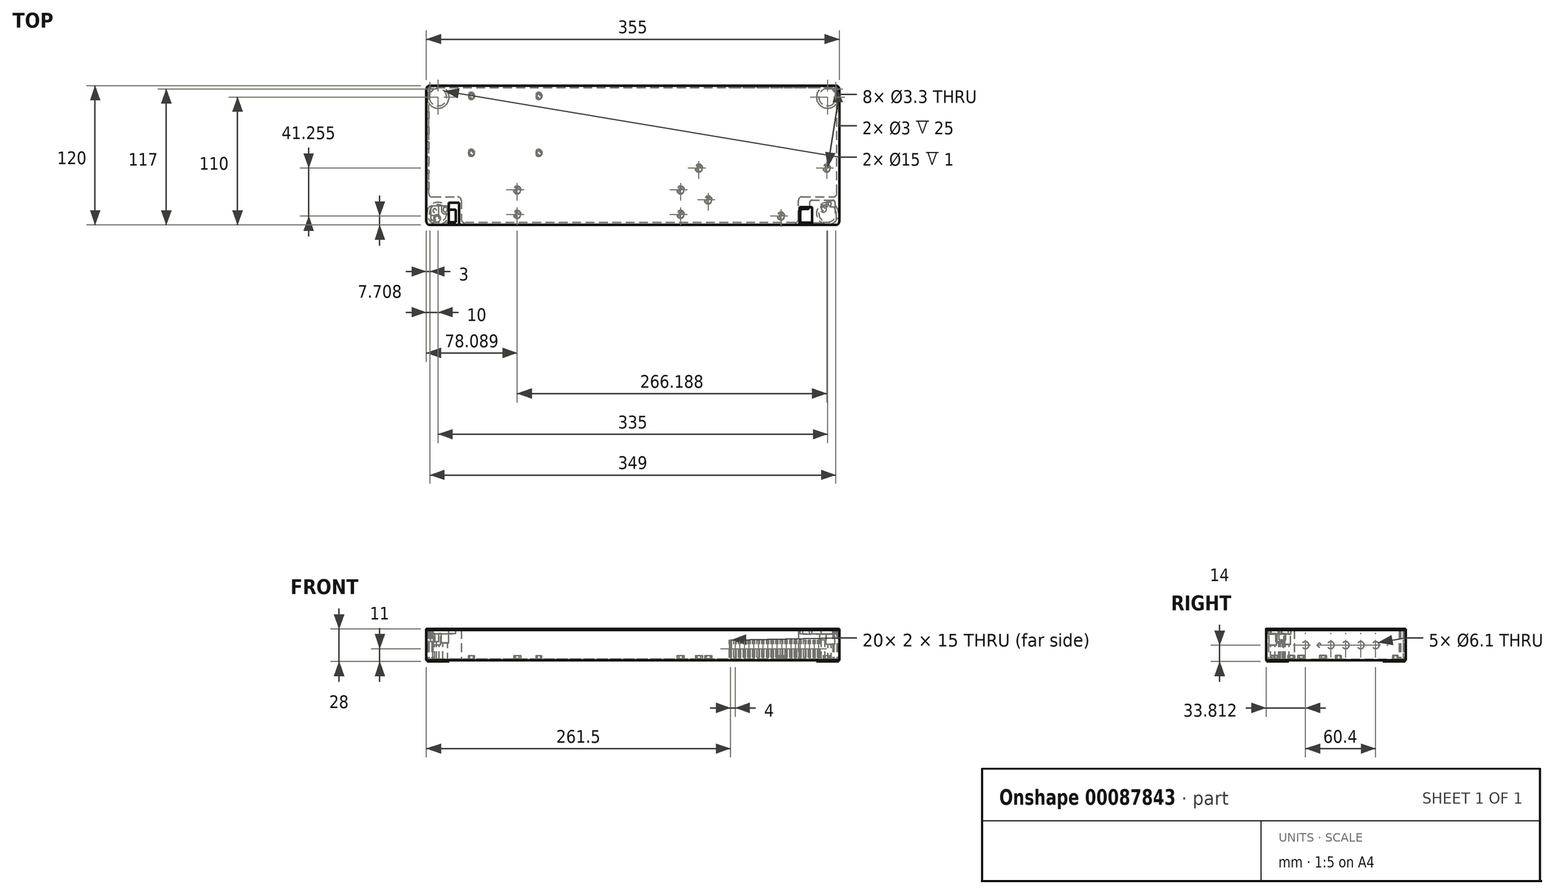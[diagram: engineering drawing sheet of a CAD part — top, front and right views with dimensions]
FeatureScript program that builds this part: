
annotation { "Feature Type Name" : "Feature", "Feature Type Description" : "" }
export const myFeature = defineFeature(function(context is Context, id is Id, definition is map)
    precondition{}
    {
        {
            var Q0;
            Q0=qCreatedBy(makeId("Top.planeOp"),FACE);
            var sketch = newSketch(context, id + "F0", { "sketchPlane" : qUnion([Q0])});
            skLineSegment(sketch, "E0.bottom", {"start": v(174.5, -60) * mm, "end": v(-174.5, -60) * mm});
            skLineSegment(sketch, "E0.top", {"start": v(174.5, 60) * mm, "end": v(-174.5, 60) * mm});
            skLineSegment(sketch, "E0.left", {"start": v(177.5, -57) * mm, "end": v(177.5, 57) * mm});
            skLineSegment(sketch, "E0.right", {"start": v(-177.5, -57) * mm, "end": v(-177.5, 57) * mm});
            skPoint(sketch, "E0.middle", {"position": v(0, 0) * mm});
            skPoint(sketch, "E1.visualSharp", {"position": v(-177.5, 60) * mm});
            skArc(sketch, "E1.filletArc", {"start": v(-174.5, 60) * mm, "mid": v(-176.62, 59.12) * mm, "end": v(-177.5, 57) * mm});
            skPoint(sketch, "E2.visualSharp", {"position": v(-177.5, -60) * mm});
            skArc(sketch, "E2.filletArc", {"start": v(-177.5, -57) * mm, "mid": v(-176.62, -59.12) * mm, "end": v(-174.5, -60) * mm});
            skPoint(sketch, "E3.visualSharp", {"position": v(177.5, -60) * mm});
            skArc(sketch, "E3.filletArc", {"start": v(174.5, -60) * mm, "mid": v(176.62, -59.12) * mm, "end": v(177.5, -57) * mm});
            skPoint(sketch, "E4.visualSharp", {"position": v(177.5, 60) * mm});
            skArc(sketch, "E4.filletArc", {"start": v(177.5, 57) * mm, "mid": v(176.62, 59.12) * mm, "end": v(174.5, 60) * mm});
            skSolve(sketch);
        }
        {
            var Q0;
            Q0=makeQuery(id+"F0.imprint","IMPRINT",FACE,{"disambiguationData":[TD([[makeQuery(id+"F0.imprint","IMPRINT",EDGE,{"derivedFrom":sQuery(id+"F0.wireOp",EDGE,"E0.bottom")}),-1.0]])]});
            extrude(context, id + "F1", {"entities" : qUnion([Q0]), "depth" : 1 * mm});
        }
        {
            var Q0;
            Q0=makeQuery(id+"F1.opExtrude","CAP_FACE",FACE,{"disambiguationData":[OSD([sQuery(id+"F0.wireOp",EDGE,"E0.bottom"),sQuery(id+"F0.wireOp",EDGE,"E0.top"),sQuery(id+"F0.wireOp",EDGE,"E0.left"),sQuery(id+"F0.wireOp",EDGE,"E0.right"),sQuery(id+"F0.wireOp",EDGE,"E1.filletArc"),sQuery(id+"F0.wireOp",EDGE,"E2.filletArc"),sQuery(id+"F0.wireOp",EDGE,"E3.filletArc"),sQuery(id+"F0.wireOp",EDGE,"E4.filletArc")])],"isStart":false});
            var sketch = newSketch(context, id + "F2", { "sketchPlane" : qUnion([Q0])});
            skLineSegment(sketch, "E5.bottom", {"start": v(174.5, -60) * mm, "end": v(-174.5, -60) * mm});
            skLineSegment(sketch, "E5.top", {"start": v(174.5, 60) * mm, "end": v(-174.5, 60) * mm});
            skLineSegment(sketch, "E5.left", {"start": v(177.5, -57) * mm, "end": v(177.5, 57) * mm});
            skLineSegment(sketch, "E5.right", {"start": v(-177.5, -57) * mm, "end": v(-177.5, 57) * mm});
            skPoint(sketch, "E5.middle", {"position": v(0, 0) * mm});
            skPoint(sketch, "E6.visualSharp", {"position": v(-177.5, 60) * mm});
            skArc(sketch, "E6.filletArc", {"start": v(-174.5, 60) * mm, "mid": v(-176.62, 59.12) * mm, "end": v(-177.5, 57) * mm});
            skPoint(sketch, "E7.visualSharp", {"position": v(-177.5, -60) * mm});
            skArc(sketch, "E7.filletArc", {"start": v(-177.5, -57) * mm, "mid": v(-176.62, -59.12) * mm, "end": v(-174.5, -60) * mm});
            skPoint(sketch, "E8.visualSharp", {"position": v(177.5, -60) * mm});
            skArc(sketch, "E8.filletArc", {"start": v(174.5, -60) * mm, "mid": v(176.62, -59.12) * mm, "end": v(177.5, -57) * mm});
            skPoint(sketch, "E9.visualSharp", {"position": v(177.5, 60) * mm});
            skArc(sketch, "E9.filletArc", {"start": v(177.5, 57) * mm, "mid": v(176.62, 59.12) * mm, "end": v(174.5, 60) * mm});
            skLineSegment(sketch, "E10.1", {"start": v(175.5, -32.82) * mm, "end": v(175.5, 54.5) * mm});
            skLineSegment(sketch, "E10.2", {"start": v(172, 58) * mm, "end": v(-172, 58) * mm});
            skLineSegment(sketch, "E10.5", {"start": v(-175.5, -32.82) * mm, "end": v(-175.5, 54.5) * mm});
            skLineSegment(sketch, "E10.7", {"start": v(139.5, -58) * mm, "end": v(-144.5, -58) * mm});
            skCircle(sketch, "E11", {"center": v(-174.5, 57) * mm, "radius": 1.5 * mm});
            skLineSegment(sketch, "E12", {"start": v(-172, 58) * mm, "end": v(-172, 57) * mm});
            skLineSegment(sketch, "E13", {"start": v(-175.5, 54.5) * mm, "end": v(-174.5, 54.5) * mm});
            skArc(sketch, "E14", {"start": v(-174.5, 54.5) * mm, "mid": v(-172.73, 55.23) * mm, "end": v(-172, 57) * mm});
            skCircle(sketch, "E15", {"center": v(174.5, 57) * mm, "radius": 1.5 * mm});
            skLineSegment(sketch, "E16", {"start": v(175.5, 54.5) * mm, "end": v(174.5, 54.5) * mm});
            skLineSegment(sketch, "E17", {"start": v(172, 58) * mm, "end": v(172, 57) * mm});
            skArc(sketch, "E18", {"start": v(172, 57) * mm, "mid": v(172.73, 55.23) * mm, "end": v(174.5, 54.5) * mm});
            skLineSegment(sketch, "E19", {"start": v(-172.5, -35.82) * mm, "end": v(-150.5, -35.82) * mm});
            skLineSegment(sketch, "E20", {"start": v(-147.5, -38.82) * mm, "end": v(-147.5, -55) * mm});
            skLineSegment(sketch, "E21", {"start": v(142.5, -55) * mm, "end": v(142.5, -38.82) * mm});
            skLineSegment(sketch, "E22", {"start": v(145.5, -35.82) * mm, "end": v(172.5, -35.82) * mm});
            skPoint(sketch, "E23.visualSharp", {"position": v(-175.5, -35.82) * mm});
            skArc(sketch, "E23.filletArc", {"start": v(-175.5, -32.82) * mm, "mid": v(-174.62, -34.94) * mm, "end": v(-172.5, -35.82) * mm});
            skPoint(sketch, "E24.visualSharp", {"position": v(-147.5, -35.82) * mm});
            skArc(sketch, "E24.filletArc", {"start": v(-147.5, -38.82) * mm, "mid": v(-148.38, -36.7) * mm, "end": v(-150.5, -35.82) * mm});
            skPoint(sketch, "E25.visualSharp", {"position": v(-147.5, -58) * mm});
            skArc(sketch, "E25.filletArc", {"start": v(-147.5, -55) * mm, "mid": v(-146.62, -57.12) * mm, "end": v(-144.5, -58) * mm});
            skPoint(sketch, "E26.visualSharp", {"position": v(142.5, -35.82) * mm});
            skArc(sketch, "E26.filletArc", {"start": v(145.5, -35.82) * mm, "mid": v(143.38, -36.7) * mm, "end": v(142.5, -38.82) * mm});
            skPoint(sketch, "E27.visualSharp", {"position": v(175.5, -35.82) * mm});
            skArc(sketch, "E27.filletArc", {"start": v(172.5, -35.82) * mm, "mid": v(174.62, -34.94) * mm, "end": v(175.5, -32.82) * mm});
            skPoint(sketch, "E28.visualSharp", {"position": v(142.5, -58) * mm});
            skArc(sketch, "E28.filletArc", {"start": v(139.5, -58) * mm, "mid": v(141.62, -57.12) * mm, "end": v(142.5, -55) * mm});
            skSolve(sketch);
        }
        {
            var Q0;
            Q0 = qSketchRegion(id + "F2", true);
            extrude(context, id + "F3", {"entities" : qUnion([Q0]), "operationType" : NewBodyOperationType.ADD, "depth" : 25 * mm});
        }
        {
            var Q0;
            Q0=makeQuery(id+"F3.boolean.opBoolean","MERGE",FACE,{"derivedFrom":[makeQuery(id+"F1.opExtrude","SWEPT_FACE",FACE,{"disambiguationData":[OSD([sQuery(id+"F0.wireOp",EDGE,"E0.top")])]}),makeQuery(id+"F3.opExtrude","SWEPT_FACE",FACE,{"disambiguationData":[OSD([sQuery(id+"F2.wireOp",EDGE,"E5.top")])]})]});
            var sketch = newSketch(context, id + "F4", { "sketchPlane" : qUnion([Q0])});
            skLineSegment(sketch, "E29.bottom", {"start": v(-159, 2.5) * mm, "end": v(-161, 2.5) * mm});
            skLineSegment(sketch, "E29.top", {"start": v(-159, 17.5) * mm, "end": v(-161, 17.5) * mm});
            skLineSegment(sketch, "E29.left", {"start": v(-159, 2.5) * mm, "end": v(-159, 17.5) * mm});
            skLineSegment(sketch, "E29.right", {"start": v(-161, 2.5) * mm, "end": v(-161, 17.5) * mm});
            skPoint(sketch, "E29.middle", {"position": v(-160, 10) * mm});
            skLineSegment(sketch, "E30.1.0.0", {"start": v(-157, 2.5) * mm, "end": v(-157, 17.5) * mm});
            skLineSegment(sketch, "E30.1.0.1", {"start": v(-155, 17.5) * mm, "end": v(-157, 17.5) * mm});
            skLineSegment(sketch, "E30.1.0.2", {"start": v(-155, 2.5) * mm, "end": v(-155, 17.5) * mm});
            skLineSegment(sketch, "E30.1.0.3", {"start": v(-155, 2.5) * mm, "end": v(-157, 2.5) * mm});
            skLineSegment(sketch, "E30.2.0.0", {"start": v(-153, 2.5) * mm, "end": v(-153, 17.5) * mm});
            skLineSegment(sketch, "E30.2.0.1", {"start": v(-151, 17.5) * mm, "end": v(-153, 17.5) * mm});
            skLineSegment(sketch, "E30.2.0.2", {"start": v(-151, 2.5) * mm, "end": v(-151, 17.5) * mm});
            skLineSegment(sketch, "E30.2.0.3", {"start": v(-151, 2.5) * mm, "end": v(-153, 2.5) * mm});
            skLineSegment(sketch, "E30.3.0.0", {"start": v(-149, 2.5) * mm, "end": v(-149, 17.5) * mm});
            skLineSegment(sketch, "E30.3.0.1", {"start": v(-147, 17.5) * mm, "end": v(-149, 17.5) * mm});
            skLineSegment(sketch, "E30.3.0.2", {"start": v(-147, 2.5) * mm, "end": v(-147, 17.5) * mm});
            skLineSegment(sketch, "E30.3.0.3", {"start": v(-147, 2.5) * mm, "end": v(-149, 2.5) * mm});
            skLineSegment(sketch, "E30.4.0.0", {"start": v(-145, 2.5) * mm, "end": v(-145, 17.5) * mm});
            skLineSegment(sketch, "E30.4.0.1", {"start": v(-143, 17.5) * mm, "end": v(-145, 17.5) * mm});
            skLineSegment(sketch, "E30.4.0.2", {"start": v(-143, 2.5) * mm, "end": v(-143, 17.5) * mm});
            skLineSegment(sketch, "E30.4.0.3", {"start": v(-143, 2.5) * mm, "end": v(-145, 2.5) * mm});
            skLineSegment(sketch, "E30.5.0.0", {"start": v(-141, 2.5) * mm, "end": v(-141, 17.5) * mm});
            skLineSegment(sketch, "E30.5.0.1", {"start": v(-139, 17.5) * mm, "end": v(-141, 17.5) * mm});
            skLineSegment(sketch, "E30.5.0.2", {"start": v(-139, 2.5) * mm, "end": v(-139, 17.5) * mm});
            skLineSegment(sketch, "E30.5.0.3", {"start": v(-139, 2.5) * mm, "end": v(-141, 2.5) * mm});
            skLineSegment(sketch, "E30.6.0.0", {"start": v(-137, 2.5) * mm, "end": v(-137, 17.5) * mm});
            skLineSegment(sketch, "E30.6.0.1", {"start": v(-135, 17.5) * mm, "end": v(-137, 17.5) * mm});
            skLineSegment(sketch, "E30.6.0.2", {"start": v(-135, 2.5) * mm, "end": v(-135, 17.5) * mm});
            skLineSegment(sketch, "E30.6.0.3", {"start": v(-135, 2.5) * mm, "end": v(-137, 2.5) * mm});
            skLineSegment(sketch, "E30.7.0.0", {"start": v(-133, 2.5) * mm, "end": v(-133, 17.5) * mm});
            skLineSegment(sketch, "E30.7.0.1", {"start": v(-131, 17.5) * mm, "end": v(-133, 17.5) * mm});
            skLineSegment(sketch, "E30.7.0.2", {"start": v(-131, 2.5) * mm, "end": v(-131, 17.5) * mm});
            skLineSegment(sketch, "E30.7.0.3", {"start": v(-131, 2.5) * mm, "end": v(-133, 2.5) * mm});
            skLineSegment(sketch, "E30.8.0.0", {"start": v(-129, 2.5) * mm, "end": v(-129, 17.5) * mm});
            skLineSegment(sketch, "E30.8.0.1", {"start": v(-127, 17.5) * mm, "end": v(-129, 17.5) * mm});
            skLineSegment(sketch, "E30.8.0.2", {"start": v(-127, 2.5) * mm, "end": v(-127, 17.5) * mm});
            skLineSegment(sketch, "E30.8.0.3", {"start": v(-127, 2.5) * mm, "end": v(-129, 2.5) * mm});
            skLineSegment(sketch, "E30.9.0.0", {"start": v(-125, 2.5) * mm, "end": v(-125, 17.5) * mm});
            skLineSegment(sketch, "E30.9.0.1", {"start": v(-123, 17.5) * mm, "end": v(-125, 17.5) * mm});
            skLineSegment(sketch, "E30.9.0.2", {"start": v(-123, 2.5) * mm, "end": v(-123, 17.5) * mm});
            skLineSegment(sketch, "E30.9.0.3", {"start": v(-123, 2.5) * mm, "end": v(-125, 2.5) * mm});
            skLineSegment(sketch, "E30.direction1", {"start": v(-161, 2.5) * mm, "end": v(-157, 2.5) * mm, "construction": true});
            skLineSegment(sketch, "E31.0.10.0", {"start": v(-121, 2.5) * mm, "end": v(-121, 17.5) * mm});
            skLineSegment(sketch, "E31.3.10.0", {"start": v(-119, 17.5) * mm, "end": v(-121, 17.5) * mm});
            skLineSegment(sketch, "E31.6.10.0", {"start": v(-119, 2.5) * mm, "end": v(-119, 17.5) * mm});
            skLineSegment(sketch, "E31.9.10.0", {"start": v(-119, 2.5) * mm, "end": v(-121, 2.5) * mm});
            skLineSegment(sketch, "E31.0.11.0", {"start": v(-117, 2.5) * mm, "end": v(-117, 17.5) * mm});
            skLineSegment(sketch, "E31.3.11.0", {"start": v(-115, 17.5) * mm, "end": v(-117, 17.5) * mm});
            skLineSegment(sketch, "E31.6.11.0", {"start": v(-115, 2.5) * mm, "end": v(-115, 17.5) * mm});
            skLineSegment(sketch, "E31.9.11.0", {"start": v(-115, 2.5) * mm, "end": v(-117, 2.5) * mm});
            skLineSegment(sketch, "E31.0.12.0", {"start": v(-113, 2.5) * mm, "end": v(-113, 17.5) * mm});
            skLineSegment(sketch, "E31.3.12.0", {"start": v(-111, 17.5) * mm, "end": v(-113, 17.5) * mm});
            skLineSegment(sketch, "E31.6.12.0", {"start": v(-111, 2.5) * mm, "end": v(-111, 17.5) * mm});
            skLineSegment(sketch, "E31.9.12.0", {"start": v(-111, 2.5) * mm, "end": v(-113, 2.5) * mm});
            skLineSegment(sketch, "E31.0.13.0", {"start": v(-109, 2.5) * mm, "end": v(-109, 17.5) * mm});
            skLineSegment(sketch, "E31.3.13.0", {"start": v(-107, 17.5) * mm, "end": v(-109, 17.5) * mm});
            skLineSegment(sketch, "E31.6.13.0", {"start": v(-107, 2.5) * mm, "end": v(-107, 17.5) * mm});
            skLineSegment(sketch, "E31.9.13.0", {"start": v(-107, 2.5) * mm, "end": v(-109, 2.5) * mm});
            skLineSegment(sketch, "E31.0.14.0", {"start": v(-105, 2.5) * mm, "end": v(-105, 17.5) * mm});
            skLineSegment(sketch, "E31.3.14.0", {"start": v(-103, 17.5) * mm, "end": v(-105, 17.5) * mm});
            skLineSegment(sketch, "E31.6.14.0", {"start": v(-103, 2.5) * mm, "end": v(-103, 17.5) * mm});
            skLineSegment(sketch, "E31.9.14.0", {"start": v(-103, 2.5) * mm, "end": v(-105, 2.5) * mm});
            skLineSegment(sketch, "E31.0.15.0", {"start": v(-101, 2.5) * mm, "end": v(-101, 17.5) * mm});
            skLineSegment(sketch, "E31.3.15.0", {"start": v(-99, 17.5) * mm, "end": v(-101, 17.5) * mm});
            skLineSegment(sketch, "E31.6.15.0", {"start": v(-99, 2.5) * mm, "end": v(-99, 17.5) * mm});
            skLineSegment(sketch, "E31.9.15.0", {"start": v(-99, 2.5) * mm, "end": v(-101, 2.5) * mm});
            skLineSegment(sketch, "E31.0.16.0", {"start": v(-97, 2.5) * mm, "end": v(-97, 17.5) * mm});
            skLineSegment(sketch, "E31.3.16.0", {"start": v(-95, 17.5) * mm, "end": v(-97, 17.5) * mm});
            skLineSegment(sketch, "E31.6.16.0", {"start": v(-95, 2.5) * mm, "end": v(-95, 17.5) * mm});
            skLineSegment(sketch, "E31.9.16.0", {"start": v(-95, 2.5) * mm, "end": v(-97, 2.5) * mm});
            skLineSegment(sketch, "E31.0.17.0", {"start": v(-93, 2.5) * mm, "end": v(-93, 17.5) * mm});
            skLineSegment(sketch, "E31.3.17.0", {"start": v(-91, 17.5) * mm, "end": v(-93, 17.5) * mm});
            skLineSegment(sketch, "E31.6.17.0", {"start": v(-91, 2.5) * mm, "end": v(-91, 17.5) * mm});
            skLineSegment(sketch, "E31.9.17.0", {"start": v(-91, 2.5) * mm, "end": v(-93, 2.5) * mm});
            skLineSegment(sketch, "E31.0.18.0", {"start": v(-89, 2.5) * mm, "end": v(-89, 17.5) * mm});
            skLineSegment(sketch, "E31.3.18.0", {"start": v(-87, 17.5) * mm, "end": v(-89, 17.5) * mm});
            skLineSegment(sketch, "E31.6.18.0", {"start": v(-87, 2.5) * mm, "end": v(-87, 17.5) * mm});
            skLineSegment(sketch, "E31.9.18.0", {"start": v(-87, 2.5) * mm, "end": v(-89, 2.5) * mm});
            skLineSegment(sketch, "E31.0.19.0", {"start": v(-85, 2.5) * mm, "end": v(-85, 17.5) * mm});
            skLineSegment(sketch, "E31.3.19.0", {"start": v(-83, 17.5) * mm, "end": v(-85, 17.5) * mm});
            skLineSegment(sketch, "E31.6.19.0", {"start": v(-83, 2.5) * mm, "end": v(-83, 17.5) * mm});
            skLineSegment(sketch, "E31.9.19.0", {"start": v(-83, 2.5) * mm, "end": v(-85, 2.5) * mm});
            skSolve(sketch);
        }
        {
            var Q0;
            Q0 = qSketchRegion(id + "F4", true);
            extrude(context, id + "F5", {"entities" : qUnion([Q0]), "operationType" : NewBodyOperationType.REMOVE, "oppositeDirection" : true, "depth" : 3 * mm});
        }
        {
            var Q0;
            Q0=makeQuery(id+"F1.opExtrude","CAP_FACE",FACE,{"disambiguationData":[OSD([sQuery(id+"F0.wireOp",EDGE,"E0.bottom"),sQuery(id+"F0.wireOp",EDGE,"E0.top"),sQuery(id+"F0.wireOp",EDGE,"E0.left"),sQuery(id+"F0.wireOp",EDGE,"E0.right"),sQuery(id+"F0.wireOp",EDGE,"E1.filletArc"),sQuery(id+"F0.wireOp",EDGE,"E2.filletArc"),sQuery(id+"F0.wireOp",EDGE,"E3.filletArc"),sQuery(id+"F0.wireOp",EDGE,"E4.filletArc")])],"isStart":true});
            var sketch = newSketch(context, id + "F6", { "sketchPlane" : qUnion([Q0])});
            skCircle(sketch, "E32", {"center": v(-167.5, 50) * mm, "radius": 7.5 * mm});
            skCircle(sketch, "E33", {"center": v(-167.5, 50) * mm, "radius": 9.5 * mm});
            skCircle(sketch, "E34.MirrorC", {"center": v(167.5, 50) * mm, "radius": 7.5 * mm});
            skCircle(sketch, "E35.MirrorC", {"center": v(167.5, 50) * mm, "radius": 9.5 * mm});
            skCircle(sketch, "E36.MirrorC", {"center": v(-167.5, -50) * mm, "radius": 7.5 * mm});
            skCircle(sketch, "E37.MirrorC", {"center": v(-167.5, -50) * mm, "radius": 9.5 * mm});
            skCircle(sketch, "E38.MirrorC", {"center": v(167.5, -50) * mm, "radius": 7.5 * mm});
            skCircle(sketch, "E39.MirrorC", {"center": v(167.5, -50) * mm, "radius": 9.5 * mm});
            skSolve(sketch);
        }
        {
            var Q0;
            Q0 = qSketchRegion(id + "F6", true);
            extrude(context, id + "F7", {"entities" : qUnion([Q0]), "operationType" : NewBodyOperationType.ADD, "depth" : 1 * mm});
        }
        {
            var Q0;
            Q0=makeQuery(id+"F3.opExtrude","CAP_FACE",FACE,{"disambiguationData":[OSD([sQuery(id+"F2.wireOp",EDGE,"E5.bottom"),sQuery(id+"F2.wireOp",EDGE,"E5.top"),sQuery(id+"F2.wireOp",EDGE,"E5.left"),sQuery(id+"F2.wireOp",EDGE,"E5.right"),sQuery(id+"F2.wireOp",EDGE,"E6.filletArc"),sQuery(id+"F2.wireOp",EDGE,"E7.filletArc"),sQuery(id+"F2.wireOp",EDGE,"E8.filletArc"),sQuery(id+"F2.wireOp",EDGE,"E9.filletArc"),sQuery(id+"F2.wireOp",EDGE,"E10.1"),sQuery(id+"F2.wireOp",EDGE,"E10.2"),sQuery(id+"F2.wireOp",EDGE,"E10.5"),sQuery(id+"F2.wireOp",EDGE,"E10.7"),sQuery(id+"F2.wireOp",EDGE,"E11"),sQuery(id+"F2.wireOp",EDGE,"E12"),sQuery(id+"F2.wireOp",EDGE,"E13"),sQuery(id+"F2.wireOp",EDGE,"E14"),sQuery(id+"F2.wireOp",EDGE,"E15"),sQuery(id+"F2.wireOp",EDGE,"E16"),sQuery(id+"F2.wireOp",EDGE,"E17"),sQuery(id+"F2.wireOp",EDGE,"E18"),sQuery(id+"F2.wireOp",EDGE,"E19"),sQuery(id+"F2.wireOp",EDGE,"E20"),sQuery(id+"F2.wireOp",EDGE,"E21"),sQuery(id+"F2.wireOp",EDGE,"E22")])],"isStart":false});
            var sketch = newSketch(context, id + "F8", { "sketchPlane" : qUnion([Q0])});
            skLineSegment(sketch, "E40", {"start": v(-173.8, -43.77) * mm, "end": v(-173.8, -57.54) * mm});
            skLineSegment(sketch, "E41", {"start": v(-173.8, -57.54) * mm, "end": v(-152.32, -57.54) * mm});
            skLineSegment(sketch, "E42", {"start": v(-152.32, -57.54) * mm, "end": v(-152.32, -46.84) * mm});
            skLineSegment(sketch, "E43", {"start": v(-152.32, -46.84) * mm, "end": v(-158.34, -46.84) * mm});
            skLineSegment(sketch, "E44", {"start": v(-158.34, -46.84) * mm, "end": v(-158.34, -43.77) * mm});
            skLineSegment(sketch, "E45", {"start": v(-158.34, -43.77) * mm, "end": v(-173.8, -43.77) * mm});
            skSolve(sketch);
        }
        {
            var Q0;
            Q0 = qSketchRegion(id + "F8", true);
            extrude(context, id + "F9", {"entities" : qUnion([Q0]), "operationType" : NewBodyOperationType.REMOVE, "oppositeDirection" : true, "depth" : 3 * mm});
        }
        {
            var Q0;
            Q0=makeQuery(id+"F9.boolean.opBoolean","COPY",FACE,{"derivedFrom":makeQuery(id+"F9.opExtrude","CAP_FACE",FACE,{"disambiguationData":[OSD([sQuery(id+"F8.wireOp",EDGE,"E40"),sQuery(id+"F8.wireOp",EDGE,"E41"),sQuery(id+"F8.wireOp",EDGE,"E42"),sQuery(id+"F8.wireOp",EDGE,"E43"),sQuery(id+"F8.wireOp",EDGE,"E44"),sQuery(id+"F8.wireOp",EDGE,"E45")])],"isStart":false})});
            var sketch = newSketch(context, id + "F10", { "sketchPlane" : qUnion([Q0])});
            skLineSegment(sketch, "E46.bottom", {"start": v(-164.52, -43.77) * mm, "end": v(-158.34, -43.77) * mm});
            skLineSegment(sketch, "E46.top", {"start": v(-161.52, -50.46) * mm, "end": v(-159.34, -50.46) * mm});
            skLineSegment(sketch, "E46.left", {"start": v(-164.52, -43.77) * mm, "end": v(-164.52, -47.46) * mm});
            skLineSegment(sketch, "E46.right", {"start": v(-158.34, -43.77) * mm, "end": v(-158.34, -49.46) * mm});
            skPoint(sketch, "E47.visualSharp", {"position": v(-164.52, -50.46) * mm});
            skArc(sketch, "E47.filletArc", {"start": v(-164.52, -47.46) * mm, "mid": v(-163.64, -49.58) * mm, "end": v(-161.52, -50.46) * mm});
            skPoint(sketch, "E48.visualSharp", {"position": v(-158.34, -50.46) * mm});
            skArc(sketch, "E48.filletArc", {"start": v(-159.34, -50.46) * mm, "mid": v(-158.63, -50.16) * mm, "end": v(-158.34, -49.46) * mm});
            skSolve(sketch);
        }
        {
            var Q0;
            Q0 = qSketchRegion(id + "F10", true);
            extrude(context, id + "F11", {"entities" : qUnion([Q0]), "operationType" : NewBodyOperationType.REMOVE, "oppositeDirection" : true, "depth" : 8 * mm});
        }
        {
            var Q0;
            Q0=makeQuery(id+"F9.boolean.opBoolean","COPY",FACE,{"derivedFrom":makeQuery(id+"F9.opExtrude","CAP_FACE",FACE,{"disambiguationData":[OSD([sQuery(id+"F8.wireOp",EDGE,"E40"),sQuery(id+"F8.wireOp",EDGE,"E41"),sQuery(id+"F8.wireOp",EDGE,"E42"),sQuery(id+"F8.wireOp",EDGE,"E43"),sQuery(id+"F8.wireOp",EDGE,"E44"),sQuery(id+"F8.wireOp",EDGE,"E45")])],"isStart":false})});
            var sketch = newSketch(context, id + "F12", { "sketchPlane" : qUnion([Q0])});
            skLineSegment(sketch, "E49", {"start": v(-173.8, -43.77) * mm, "end": v(-173.8, -51.65) * mm});
            skLineSegment(sketch, "E50", {"start": v(-173.8, -51.65) * mm, "end": v(-166.73, -51.65) * mm});
            skLineSegment(sketch, "E51", {"start": v(-166.73, -51.65) * mm, "end": v(-166.73, -43.77) * mm});
            skLineSegment(sketch, "E52", {"start": v(-166.73, -43.77) * mm, "end": v(-173.8, -43.77) * mm});
            skSolve(sketch);
        }
        {
            var Q0;
            Q0 = qSketchRegion(id + "F12", true);
            extrude(context, id + "F13", {"entities" : qUnion([Q0]), "operationType" : NewBodyOperationType.REMOVE, "oppositeDirection" : true, "depth" : 7 * mm});
        }
        {
            var Q0;
            Q0=makeQuery(id+"F9.boolean.opBoolean","COPY",FACE,{"derivedFrom":makeQuery(id+"F9.opExtrude","CAP_FACE",FACE,{"disambiguationData":[OSD([sQuery(id+"F8.wireOp",EDGE,"E40"),sQuery(id+"F8.wireOp",EDGE,"E41"),sQuery(id+"F8.wireOp",EDGE,"E42"),sQuery(id+"F8.wireOp",EDGE,"E43"),sQuery(id+"F8.wireOp",EDGE,"E44"),sQuery(id+"F8.wireOp",EDGE,"E45")])],"isStart":false})});
            var sketch = newSketch(context, id + "F14", { "sketchPlane" : qUnion([Q0])});
            skCircle(sketch, "E53", {"center": v(-168.35, -54.25) * mm, "radius": 3.07 * mm});
            skSolve(sketch);
        }
        {
            var Q0;
            Q0 = qSketchRegion(id + "F14", true);
            extrude(context, id + "F15", {"entities" : qUnion([Q0]), "operationType" : NewBodyOperationType.REMOVE, "oppositeDirection" : true, "depth" : 10 * mm});
        }
        {
            var Q0;
            Q0=makeQuery(id+"F11.boolean.opBoolean","COPY",FACE,{"derivedFrom":makeQuery(id+"F11.opExtrude","CAP_FACE",FACE,{"disambiguationData":[OSD([sQuery(id+"F10.wireOp",EDGE,"E46.bottom"),sQuery(id+"F10.wireOp",EDGE,"E46.top"),sQuery(id+"F10.wireOp",EDGE,"E46.left"),sQuery(id+"F10.wireOp",EDGE,"E46.right"),sQuery(id+"F10.wireOp",EDGE,"E47.filletArc"),sQuery(id+"F10.wireOp",EDGE,"E48.filletArc")])],"isStart":false})});
            var sketch = newSketch(context, id + "F16", { "sketchPlane" : qUnion([Q0])});
            skCircle(sketch, "E54", {"center": v(-161.28, -46.78) * mm, "radius": 1.92 * mm});
            skSolve(sketch);
        }
        {
            var Q0;
            Q0 = qSketchRegion(id + "F16", true);
            extrude(context, id + "F17", {"entities" : qUnion([Q0]), "operationType" : NewBodyOperationType.REMOVE, "endBound" : BoundingType.THROUGH_ALL, "oppositeDirection" : true, "depth" : 25 * mm});
        }
        {
            var Q0;
            Q0=makeQuery(id+"F13.boolean.opBoolean","COPY",FACE,{"derivedFrom":makeQuery(id+"F13.opExtrude","CAP_FACE",FACE,{"disambiguationData":[OSD([sQuery(id+"F12.wireOp",EDGE,"E49"),sQuery(id+"F12.wireOp",EDGE,"E50"),sQuery(id+"F12.wireOp",EDGE,"E51"),sQuery(id+"F12.wireOp",EDGE,"E52")])],"isStart":false})});
            var sketch = newSketch(context, id + "F18", { "sketchPlane" : qUnion([Q0])});
            skCircle(sketch, "E55", {"center": v(-170.4, -47.59) * mm, "radius": 1.6 * mm});
            skSolve(sketch);
        }
        {
            var Q0;
            Q0 = qSketchRegion(id + "F18", true);
            extrude(context, id + "F19", {"entities" : qUnion([Q0]), "operationType" : NewBodyOperationType.REMOVE, "endBound" : BoundingType.THROUGH_ALL, "oppositeDirection" : true, "depth" : 25 * mm});
        }
        {
            var Q0;
            Q0=makeQuery(id+"F15.boolean.opBoolean","COPY",FACE,{"derivedFrom":makeQuery(id+"F15.opExtrude","CAP_FACE",FACE,{"disambiguationData":[OSD([sQuery(id+"F14.wireOp",EDGE,"E53")])],"isStart":false})});
            var sketch = newSketch(context, id + "F20", { "sketchPlane" : qUnion([Q0])});
            skCircle(sketch, "E56", {"center": v(-168.35, -54.25) * mm, "radius": 1.9 * mm});
            skSolve(sketch);
        }
        {
            var Q0;
            Q0 = qSketchRegion(id + "F20", true);
            extrude(context, id + "F21", {"entities" : qUnion([Q0]), "operationType" : NewBodyOperationType.REMOVE, "endBound" : BoundingType.THROUGH_ALL, "oppositeDirection" : true, "depth" : 25 * mm});
        }
        {
            var Q0;
            Q0=makeQuery(id+"F3.opExtrude","CAP_FACE",FACE,{"disambiguationData":[OSD([sQuery(id+"F2.wireOp",EDGE,"E5.bottom"),sQuery(id+"F2.wireOp",EDGE,"E5.top"),sQuery(id+"F2.wireOp",EDGE,"E5.left"),sQuery(id+"F2.wireOp",EDGE,"E5.right"),sQuery(id+"F2.wireOp",EDGE,"E6.filletArc"),sQuery(id+"F2.wireOp",EDGE,"E7.filletArc"),sQuery(id+"F2.wireOp",EDGE,"E8.filletArc"),sQuery(id+"F2.wireOp",EDGE,"E9.filletArc"),sQuery(id+"F2.wireOp",EDGE,"E10.1"),sQuery(id+"F2.wireOp",EDGE,"E10.2"),sQuery(id+"F2.wireOp",EDGE,"E10.5"),sQuery(id+"F2.wireOp",EDGE,"E10.7"),sQuery(id+"F2.wireOp",EDGE,"E11"),sQuery(id+"F2.wireOp",EDGE,"E12"),sQuery(id+"F2.wireOp",EDGE,"E13"),sQuery(id+"F2.wireOp",EDGE,"E14"),sQuery(id+"F2.wireOp",EDGE,"E15"),sQuery(id+"F2.wireOp",EDGE,"E16"),sQuery(id+"F2.wireOp",EDGE,"E17"),sQuery(id+"F2.wireOp",EDGE,"E18"),sQuery(id+"F2.wireOp",EDGE,"E19"),sQuery(id+"F2.wireOp",EDGE,"E20"),sQuery(id+"F2.wireOp",EDGE,"E21"),sQuery(id+"F2.wireOp",EDGE,"E22")])],"isStart":false});
            var sketch = newSketch(context, id + "F22", { "sketchPlane" : qUnion([Q0])});
            skArc(sketch, "E57.0", {"start": v(174.05, -40.84) * mm, "mid": v(173.47, -39.33) * mm, "end": v(171.95, -38.74) * mm});
            skLineSegment(sketch, "E57.1", {"start": v(174.05, -49.54) * mm, "end": v(174.05, -40.84) * mm});
            skLineSegment(sketch, "E57.2", {"start": v(175.05, -49.54) * mm, "end": v(174.05, -49.54) * mm});
            skLineSegment(sketch, "E57.3", {"start": v(175.05, -55.44) * mm, "end": v(175.05, -49.54) * mm});
            skArc(sketch, "E57.4", {"start": v(146.15, -46.34) * mm, "mid": v(144.64, -46.93) * mm, "end": v(144.05, -48.44) * mm});
            skLineSegment(sketch, "E57.5", {"start": v(150.05, -46.34) * mm, "end": v(146.15, -46.34) * mm});
            skLineSegment(sketch, "E57.6", {"start": v(152.05, -40.84) * mm, "end": v(152.05, -44.34) * mm});
            skArc(sketch, "E57.7", {"start": v(154.15, -38.74) * mm, "mid": v(152.64, -39.33) * mm, "end": v(152.05, -40.84) * mm});
            skLineSegment(sketch, "E57.8", {"start": v(144.05, -48.44) * mm, "end": v(144.05, -55.94) * mm});
            skArc(sketch, "E57.9", {"start": v(144.05, -55.94) * mm, "mid": v(144.64, -57.46) * mm, "end": v(146.15, -58.04) * mm});
            skLineSegment(sketch, "E57.10", {"start": v(146.15, -58.04) * mm, "end": v(162.25, -58.04) * mm});
            skLineSegment(sketch, "E57.11", {"start": v(162.25, -58.04) * mm, "end": v(162.25, -57.54) * mm});
            skLineSegment(sketch, "E57.12", {"start": v(171.95, -38.74) * mm, "end": v(154.15, -38.74) * mm});
            skLineSegment(sketch, "E57.13", {"start": v(162.25, -57.54) * mm, "end": v(172.95, -57.54) * mm});
            skArc(sketch, "E57.14", {"start": v(172.95, -57.54) * mm, "mid": v(174.47, -56.96) * mm, "end": v(175.05, -55.44) * mm});
            skArc(sketch, "E58.filletArc", {"start": v(150.05, -46.34) * mm, "mid": v(151.47, -45.76) * mm, "end": v(152.05, -44.34) * mm});
            skSolve(sketch);
        }
        {
            var Q0;
            Q0=makeQuery(id+"F22.imprint","IMPRINT",FACE,{"disambiguationData":[TD([[makeQuery(id+"F22.imprint","IMPRINT",EDGE,{"derivedFrom":sQuery(id+"F22.wireOp",EDGE,"E57.0")}),1.0]])]});
            extrude(context, id + "F23", {"entities" : qUnion([Q0]), "operationType" : NewBodyOperationType.REMOVE, "oppositeDirection" : true, "depth" : 3.5 * mm});
        }
        {
            var Q0;
            Q0=makeQuery(id+"F23.boolean.opBoolean","COPY",FACE,{"derivedFrom":makeQuery(id+"F23.opExtrude","CAP_FACE",FACE,{"disambiguationData":[OSD([sQuery(id+"F22.wireOp",EDGE,"E57.0"),sQuery(id+"F22.wireOp",EDGE,"E57.1"),sQuery(id+"F22.wireOp",EDGE,"E57.2"),sQuery(id+"F22.wireOp",EDGE,"E57.3"),sQuery(id+"F22.wireOp",EDGE,"E57.4"),sQuery(id+"F22.wireOp",EDGE,"E57.5"),sQuery(id+"F22.wireOp",EDGE,"E57.6"),sQuery(id+"F22.wireOp",EDGE,"E57.7"),sQuery(id+"F22.wireOp",EDGE,"E57.8"),sQuery(id+"F22.wireOp",EDGE,"E57.9"),sQuery(id+"F22.wireOp",EDGE,"E57.10"),sQuery(id+"F22.wireOp",EDGE,"E57.11"),sQuery(id+"F22.wireOp",EDGE,"E57.12"),sQuery(id+"F22.wireOp",EDGE,"E57.13"),sQuery(id+"F22.wireOp",EDGE,"E57.14"),sQuery(id+"F22.wireOp",EDGE,"E58.filletArc")])],"isStart":false})});
            var sketch = newSketch(context, id + "F24", { "sketchPlane" : qUnion([Q0])});
            skLineSegment(sketch, "E59", {"start": v(173.95, -44.74) * mm, "end": v(169.3, -44.74) * mm});
            skLineSegment(sketch, "E60", {"start": v(166.35, -41.8) * mm, "end": v(166.35, -41.8) * mm});
            skLineSegment(sketch, "E61", {"start": v(169.3, -38.84) * mm, "end": v(171.95, -38.84) * mm});
            skLineSegment(sketch, "E62", {"start": v(173.95, -40.84) * mm, "end": v(173.95, -44.74) * mm});
            skPoint(sketch, "E63.visualSharp", {"position": v(173.95, -38.84) * mm});
            skArc(sketch, "E63.filletArc", {"start": v(173.95, -40.84) * mm, "mid": v(173.37, -39.43) * mm, "end": v(171.95, -38.84) * mm});
            skPoint(sketch, "E64.visualSharp", {"position": v(166.35, -38.84) * mm});
            skArc(sketch, "E64.filletArc", {"start": v(169.3, -38.84) * mm, "mid": v(167.22, -39.7) * mm, "end": v(166.35, -41.8) * mm});
            skPoint(sketch, "E65.visualSharp", {"position": v(166.35, -44.74) * mm});
            skArc(sketch, "E65.filletArc", {"start": v(166.35, -41.8) * mm, "mid": v(167.22, -43.88) * mm, "end": v(169.3, -44.74) * mm});
            skSolve(sketch);
        }
        {
            var Q0;
            Q0 = qSketchRegion(id + "F24", true);
            extrude(context, id + "F25", {"entities" : qUnion([Q0]), "operationType" : NewBodyOperationType.REMOVE, "oppositeDirection" : true, "depth" : 8.9 * mm});
        }
        {
            var Q0;
            Q0=makeQuery(id+"F25.boolean.opBoolean","COPY",FACE,{"derivedFrom":makeQuery(id+"F25.opExtrude","CAP_FACE",FACE,{"disambiguationData":[OSD([sQuery(id+"F24.wireOp",EDGE,"E59"),sQuery(id+"F24.wireOp",EDGE,"E61"),sQuery(id+"F24.wireOp",EDGE,"E62"),sQuery(id+"F24.wireOp",EDGE,"E63.filletArc"),sQuery(id+"F24.wireOp",EDGE,"E64.filletArc"),sQuery(id+"F24.wireOp",EDGE,"E65.filletArc")])],"isStart":false})});
            var sketch = newSketch(context, id + "F26", { "sketchPlane" : qUnion([Q0])});
            skCircle(sketch, "E66", {"center": v(169.3, -41.8) * mm, "radius": 1.5 * mm});
            skSolve(sketch);
        }
        {
            var Q0;
            Q0 = qSketchRegion(id + "F26", true);
            extrude(context, id + "F27", {"entities" : qUnion([Q0]), "operationType" : NewBodyOperationType.REMOVE, "endBound" : BoundingType.THROUGH_ALL, "oppositeDirection" : true, "depth" : 25 * mm});
        }
        {
            var Q0;
            Q0=makeQuery(id+"F23.boolean.opBoolean","COPY",FACE,{"derivedFrom":makeQuery(id+"F23.opExtrude","CAP_FACE",FACE,{"disambiguationData":[OSD([sQuery(id+"F22.wireOp",EDGE,"E57.0"),sQuery(id+"F22.wireOp",EDGE,"E57.1"),sQuery(id+"F22.wireOp",EDGE,"E57.2"),sQuery(id+"F22.wireOp",EDGE,"E57.3"),sQuery(id+"F22.wireOp",EDGE,"E57.4"),sQuery(id+"F22.wireOp",EDGE,"E57.5"),sQuery(id+"F22.wireOp",EDGE,"E57.6"),sQuery(id+"F22.wireOp",EDGE,"E57.7"),sQuery(id+"F22.wireOp",EDGE,"E57.8"),sQuery(id+"F22.wireOp",EDGE,"E57.9"),sQuery(id+"F22.wireOp",EDGE,"E57.10"),sQuery(id+"F22.wireOp",EDGE,"E57.11"),sQuery(id+"F22.wireOp",EDGE,"E57.12"),sQuery(id+"F22.wireOp",EDGE,"E57.13"),sQuery(id+"F22.wireOp",EDGE,"E57.14"),sQuery(id+"F22.wireOp",EDGE,"E58.filletArc")])],"isStart":false})});
            var sketch = newSketch(context, id + "F28", { "sketchPlane" : qUnion([Q0])});
            skCircle(sketch, "E67", {"center": v(163.74, -46) * mm, "radius": 2.92 * mm});
            skSolve(sketch);
        }
        {
            var Q0;
            Q0=makeQuery(id+"F28.imprint","IMPRINT",FACE,{"disambiguationData":[TD([[makeQuery(id+"F28.imprint","IMPRINT",EDGE,{"derivedFrom":sQuery(id+"F28.wireOp",EDGE,"E67")}),1.0]])]});
            extrude(context, id + "F29", {"entities" : qUnion([Q0]), "operationType" : NewBodyOperationType.REMOVE, "oppositeDirection" : true, "depth" : 5 * mm});
        }
        {
            var Q0;
            Q0=makeQuery(id+"F29.boolean.opBoolean","COPY",FACE,{"derivedFrom":makeQuery(id+"F29.opExtrude","CAP_FACE",FACE,{"disambiguationData":[OSD([sQuery(id+"F28.wireOp",EDGE,"E67")])],"isStart":false})});
            var sketch = newSketch(context, id + "F30", { "sketchPlane" : qUnion([Q0])});
            skCircle(sketch, "E68", {"center": v(163.74, -46) * mm, "radius": 1.5 * mm});
            skSolve(sketch);
        }
        {
            var Q0;
            Q0 = qSketchRegion(id + "F30", true);
            extrude(context, id + "F31", {"entities" : qUnion([Q0]), "operationType" : NewBodyOperationType.REMOVE, "endBound" : BoundingType.THROUGH_ALL, "oppositeDirection" : true, "depth" : 25 * mm});
        }
        {
            var Q0;
            Q0=makeQuery(id+"F3.opExtrude","CAP_FACE",FACE,{"disambiguationData":[OSD([sQuery(id+"F2.wireOp",EDGE,"E5.bottom"),sQuery(id+"F2.wireOp",EDGE,"E5.top"),sQuery(id+"F2.wireOp",EDGE,"E5.left"),sQuery(id+"F2.wireOp",EDGE,"E5.right"),sQuery(id+"F2.wireOp",EDGE,"E6.filletArc"),sQuery(id+"F2.wireOp",EDGE,"E7.filletArc"),sQuery(id+"F2.wireOp",EDGE,"E8.filletArc"),sQuery(id+"F2.wireOp",EDGE,"E9.filletArc"),sQuery(id+"F2.wireOp",EDGE,"E10.1"),sQuery(id+"F2.wireOp",EDGE,"E10.2"),sQuery(id+"F2.wireOp",EDGE,"E10.5"),sQuery(id+"F2.wireOp",EDGE,"E10.7"),sQuery(id+"F2.wireOp",EDGE,"E11"),sQuery(id+"F2.wireOp",EDGE,"E12"),sQuery(id+"F2.wireOp",EDGE,"E13"),sQuery(id+"F2.wireOp",EDGE,"E14"),sQuery(id+"F2.wireOp",EDGE,"E15"),sQuery(id+"F2.wireOp",EDGE,"E16"),sQuery(id+"F2.wireOp",EDGE,"E17"),sQuery(id+"F2.wireOp",EDGE,"E18"),sQuery(id+"F2.wireOp",EDGE,"E19"),sQuery(id+"F2.wireOp",EDGE,"E20"),sQuery(id+"F2.wireOp",EDGE,"E21"),sQuery(id+"F2.wireOp",EDGE,"E22")])],"isStart":false});
            var sketch = newSketch(context, id + "F32", { "sketchPlane" : qUnion([Q0])});
            skLineSegment(sketch, "E69", {"start": v(-177.5, 57) * mm, "end": v(-177.5, -57) * mm});
            skLineSegment(sketch, "E70", {"start": v(-174.5, -60) * mm, "end": v(-158.32, -60) * mm});
            skLineSegment(sketch, "E71", {"start": v(-158.32, -60) * mm, "end": v(-158.32, -40.84) * mm});
            skLineSegment(sketch, "E72", {"start": v(-158.32, -40.84) * mm, "end": v(-149.22, -40.84) * mm});
            skLineSegment(sketch, "E73", {"start": v(-149.22, -40.84) * mm, "end": v(-149.22, -60) * mm});
            skLineSegment(sketch, "E74", {"start": v(-149.22, -60) * mm, "end": v(143.39, -60) * mm});
            skLineSegment(sketch, "E75", {"start": v(143.39, -60) * mm, "end": v(143.39, -44.67) * mm});
            skLineSegment(sketch, "E76", {"start": v(143.39, -44.67) * mm, "end": v(154.24, -44.67) * mm});
            skLineSegment(sketch, "E77", {"start": v(154.24, -44.67) * mm, "end": v(154.24, -60) * mm});
            skLineSegment(sketch, "E78", {"start": v(154.24, -60) * mm, "end": v(174.5, -60) * mm});
            skLineSegment(sketch, "E79", {"start": v(177.5, -57) * mm, "end": v(177.5, 57) * mm});
            skLineSegment(sketch, "E80", {"start": v(174.5, 60) * mm, "end": v(-174.5, 60) * mm});
            skPoint(sketch, "E81.visualSharp", {"position": v(-177.5, 60) * mm});
            skArc(sketch, "E81.filletArc", {"start": v(-174.5, 60) * mm, "mid": v(-176.62, 59.12) * mm, "end": v(-177.5, 57) * mm});
            skPoint(sketch, "E82.visualSharp", {"position": v(177.5, 60) * mm});
            skArc(sketch, "E82.filletArc", {"start": v(177.5, 57) * mm, "mid": v(176.62, 59.12) * mm, "end": v(174.5, 60) * mm});
            skPoint(sketch, "E83.visualSharp", {"position": v(177.5, -60) * mm});
            skArc(sketch, "E83.filletArc", {"start": v(174.5, -60) * mm, "mid": v(176.62, -59.12) * mm, "end": v(177.5, -57) * mm});
            skPoint(sketch, "E84.visualSharp", {"position": v(-177.5, -60) * mm});
            skArc(sketch, "E84.filletArc", {"start": v(-177.5, -57) * mm, "mid": v(-176.62, -59.12) * mm, "end": v(-174.5, -60) * mm});
            skSolve(sketch);
        }
        {
            var Q0;
            Q0 = qSketchRegion(id + "F32", true);
            extrude(context, id + "F33", {"entities" : qUnion([Q0]), "depth" : 1 * mm});
        }
        {
            var Q0;
            Q0=makeQuery(id+"F3.boolean.opBoolean","MERGE",FACE,{"derivedFrom":[makeQuery(id+"F1.opExtrude","SWEPT_FACE",FACE,{"disambiguationData":[OSD([sQuery(id+"F0.wireOp",EDGE,"E0.right")])]}),makeQuery(id+"F3.opExtrude","SWEPT_FACE",FACE,{"disambiguationData":[OSD([sQuery(id+"F2.wireOp",EDGE,"E5.right")])]})]});
            var sketch = newSketch(context, id + "F34", { "sketchPlane" : qUnion([Q0])});
            skCircle(sketch, "E85", {"center": v(-34.21, 13) * mm, "radius": 3.05 * mm});
            skCircle(sketch, "E86", {"center": v(-21.31, 13) * mm, "radius": 3.05 * mm});
            skCircle(sketch, "E87", {"center": v(-8.41, 13) * mm, "radius": 3.05 * mm});
            skCircle(sketch, "E88", {"center": v(4.49, 13) * mm, "radius": 3.05 * mm});
            skCircle(sketch, "E89", {"center": v(14.24, 13) * mm, "radius": 1.5 * mm});
            skCircle(sketch, "E90", {"center": v(26.19, 13) * mm, "radius": 3.05 * mm});
            skPoint(sketch, "E91", {"position": v(-57, 13) * mm});
            skSolve(sketch);
        }
        {
            var Q0;
            Q0 = qSketchRegion(id + "F34", true);
            extrude(context, id + "F35", {"entities" : qUnion([Q0]), "operationType" : NewBodyOperationType.REMOVE, "endBound" : BoundingType.UP_TO_NEXT, "oppositeDirection" : true, "depth" : 25 * mm});
        }
        {
            var Q0;
            {var subQ0=sQuery(id+"F0.wireOp",EDGE,"E4.filletArc");var subQ1=sQuery(id+"F0.wireOp",EDGE,"E3.filletArc");var subQ2=sQuery(id+"F0.wireOp",EDGE,"E2.filletArc");var subQ3=sQuery(id+"F0.wireOp",EDGE,"E1.filletArc");var subQ4=sQuery(id+"F0.wireOp",EDGE,"E0.bottom");var subQ5=sQuery(id+"F0.wireOp",EDGE,"E0.top");var subQ6=sQuery(id+"F0.wireOp",EDGE,"E0.left");var subQ7=sQuery(id+"F0.wireOp",EDGE,"E0.right");Q0=makeQuery(id+"F7.boolean.opBoolean","SPLIT",FACE,{"disambiguationData":[TD([makeQuery(id+"F1.opExtrude","SWEPT_FACE",FACE,{"disambiguationData":[OSD([subQ4])]})])],"derivedFrom":makeQuery(id+"F1.opExtrude","CAP_FACE",FACE,{"disambiguationData":[OSD([subQ4,subQ5,subQ6,subQ7,subQ3,subQ2,subQ1,subQ0])],"isStart":true})});}
            var sketch = newSketch(context, id + "F36", { "sketchPlane" : qUnion([Q0])});
            skCircle(sketch, "E92", {"center": v(-138.91, -2.1) * mm, "radius": 2.5 * mm});
            skCircle(sketch, "E93", {"center": v(-80.91, -2.1) * mm, "radius": 2.5 * mm});
            skCircle(sketch, "E94", {"center": v(-138.91, -51.1) * mm, "radius": 2.5 * mm});
            skCircle(sketch, "E95", {"center": v(-80.91, -51.1) * mm, "radius": 2.5 * mm});
            skCircle(sketch, "E96", {"center": v(-99.41, 50.84) * mm, "radius": 3 * mm});
            skCircle(sketch, "E97", {"center": v(41.09, 50.84) * mm, "radius": 3 * mm});
            skCircle(sketch, "E98", {"center": v(-99.41, 29.84) * mm, "radius": 3 * mm});
            skCircle(sketch, "E99", {"center": v(41.09, 29.84) * mm, "radius": 3 * mm});
            skCircle(sketch, "E100", {"center": v(64.8, 38.4) * mm, "radius": 3 * mm});
            skPoint(sketch, "E101", {"position": v(64.8, 52.3) * mm});
            skPoint(sketch, "E102", {"position": v(127.4, 38.4) * mm});
            skCircle(sketch, "E103", {"center": v(127.4, 52.3) * mm, "radius": 3 * mm});
            skCircle(sketch, "E104", {"center": v(56.78, 11.04) * mm, "radius": 3 * mm});
            skCircle(sketch, "E105", {"center": v(166.78, 11.04) * mm, "radius": 3 * mm});
            skSolve(sketch);
        }
        {
            var Q0;
            Q0 = qSketchRegion(id + "F36", true);
            extrude(context, id + "F37", {"entities" : qUnion([Q0]), "operationType" : NewBodyOperationType.ADD, "oppositeDirection" : true, "depth" : 4 * mm});
        }
        {
            var Q0;
            Q0=sQuery(id+"F36.wireOp",VERTEX,"E92.center");
            var Q1;
            Q1=sQuery(id+"F36.wireOp",VERTEX,"E93.center");
            var Q2;
            Q2=sQuery(id+"F36.wireOp",VERTEX,"E94.center");
            var Q3;
            Q3=sQuery(id+"F36.wireOp",VERTEX,"E95.center");
            var Q4;
            Q4=makeQuery(id+"F1.opExtrude","SWEPT_BODY",BODY,{"disambiguationData":[OSD([sQuery(id+"F0.wireOp",EDGE,"E0.bottom"),sQuery(id+"F0.wireOp",EDGE,"E0.top"),sQuery(id+"F0.wireOp",EDGE,"E0.left"),sQuery(id+"F0.wireOp",EDGE,"E0.right"),sQuery(id+"F0.wireOp",EDGE,"E1.filletArc"),sQuery(id+"F0.wireOp",EDGE,"E2.filletArc"),sQuery(id+"F0.wireOp",EDGE,"E3.filletArc"),sQuery(id+"F0.wireOp",EDGE,"E4.filletArc")])]});
            hole(context, id + "F38", {"style" : HoleStyle.C_BORE, "endStyle" : HoleEndStyle.THROUGH, "holeDiameter" : 3 * mm, "cBoreDiameter" : 6 * mm, "cBoreDepth" : 0.5 * mm, "tappedDepth" : 12 * mm, "tapClearance" : 3, "startFromSketch" : true, "locations" : qUnion([Q0, Q1, Q2, Q3]), "scope" : qUnion([Q4])});
        }
        {
            var Q0;
            Q0=sQuery(id+"F36.wireOp",VERTEX,"E96.center");
            var Q1;
            Q1=sQuery(id+"F36.wireOp",VERTEX,"E98.center");
            var Q2;
            Q2=sQuery(id+"F36.wireOp",VERTEX,"E97.center");
            var Q3;
            Q3=sQuery(id+"F36.wireOp",VERTEX,"E99.center");
            var Q4;
            Q4=sQuery(id+"F36.wireOp",VERTEX,"E100.center");
            var Q5;
            Q5=sQuery(id+"F36.wireOp",VERTEX,"E103.center");
            var Q6;
            Q6=sQuery(id+"F36.wireOp",VERTEX,"E104.center");
            var Q7;
            Q7=sQuery(id+"F36.wireOp",VERTEX,"E105.center");
            var Q8;
            Q8=makeQuery(id+"F1.opExtrude","SWEPT_BODY",BODY,{"disambiguationData":[OSD([sQuery(id+"F0.wireOp",EDGE,"E0.bottom"),sQuery(id+"F0.wireOp",EDGE,"E0.top"),sQuery(id+"F0.wireOp",EDGE,"E0.left"),sQuery(id+"F0.wireOp",EDGE,"E0.right"),sQuery(id+"F0.wireOp",EDGE,"E1.filletArc"),sQuery(id+"F0.wireOp",EDGE,"E2.filletArc"),sQuery(id+"F0.wireOp",EDGE,"E3.filletArc"),sQuery(id+"F0.wireOp",EDGE,"E4.filletArc")])]});
            hole(context, id + "F39", {"style" : HoleStyle.C_SINK, "endStyle" : HoleEndStyle.THROUGH, "standardTappedOrClearance" : lookupTablePath({ "standard" : "ISO", "fit" : "Normal", "size" : "M3", "type" : "Clearance" }), "standardBlindInLast" : lookupTablePath({ "fit" : "Standard", "standard" : "ISO", "size" : "M3", "type" : "Clearance" }), "holeDiameter" : 3.3 * mm, "cSinkDiameter" : 6.72 * mm, "cSinkAngle" : 90 * degree, "tappedDepth" : 12 * mm, "tapClearance" : 3, "startFromSketch" : true, "locations" : qUnion([Q0, Q1, Q2, Q3, Q4, Q5, Q6, Q7]), "scope" : qUnion([Q8])});
        }
    });
